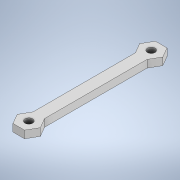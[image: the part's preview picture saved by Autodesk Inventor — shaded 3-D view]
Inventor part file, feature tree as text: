
AUTODESK INVENTOR PART (.ipt)
format: ipt  version: 2020 (Build 240168000, 168)  size: 121,344 bytes
history: native  units: in
note: dims shown in document units (in); Inventor stores cm internally (conversion verified against a paired STEP export)
features: extrude x1, sketch x1
ambient origin geometry x8: Origin, YZ Plane, XZ Plane, XY Plane, X Axis, Y Axis, Z Axis, Center Point
bodies: Solid1 (feature_tree)
feature tree (2):
  extrude  "Extrusion1"  Depth=0.315in
  sketch  "Sketch1"  dims[d1=1.6142in d2=0.315in d3=0.122in d4=0.122in d5=0.1181in d6=0.0in]
